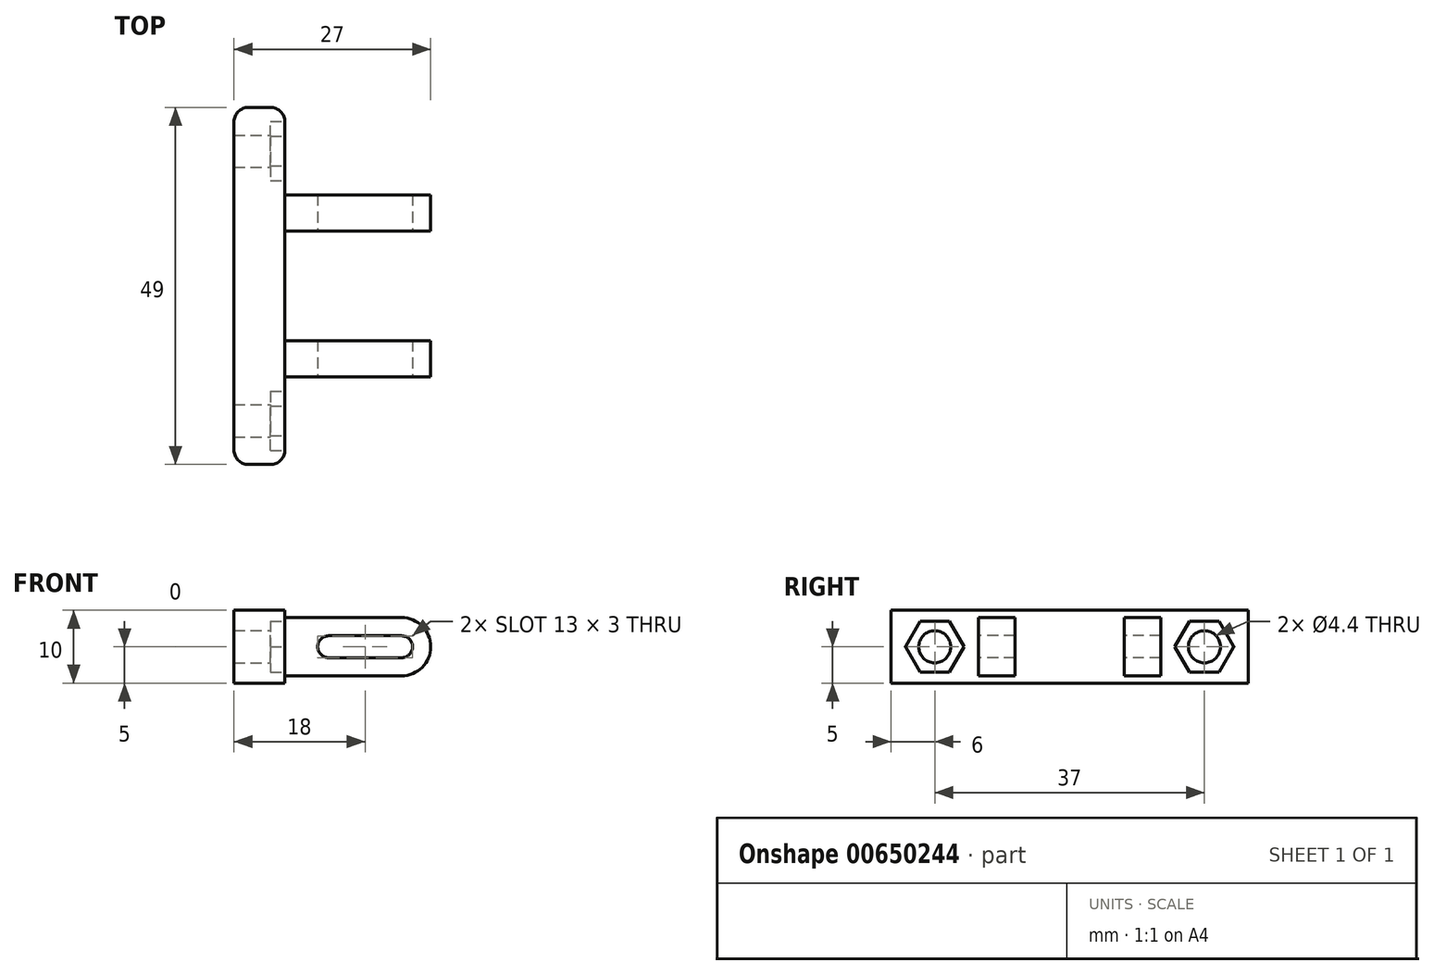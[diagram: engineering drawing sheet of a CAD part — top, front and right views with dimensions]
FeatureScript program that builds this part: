
annotation { "Feature Type Name" : "Feature", "Feature Type Description" : "" }
export const myFeature = defineFeature(function(context is Context, id is Id, definition is map)
    precondition{}
    {
        {
            var Q0;
            Q0=qCreatedBy(makeId("Top.planeOp"),FACE);
            var sketch = newSketch(context, id + "F0", { "sketchPlane" : qUnion([Q0])});
            skLineSegment(sketch, "E0", {"start": v(0, 0) * mm, "end": v(7, 0) * mm});
            skLineSegment(sketch, "E1", {"start": v(7, 0) * mm, "end": v(7, 12) * mm});
            skLineSegment(sketch, "E2", {"start": v(7, 12) * mm, "end": v(27, 12) * mm});
            skLineSegment(sketch, "E3", {"start": v(27, 12) * mm, "end": v(27, 17) * mm});
            skLineSegment(sketch, "E4", {"start": v(27, 17) * mm, "end": v(7, 17) * mm});
            skLineSegment(sketch, "E5", {"start": v(7, 17) * mm, "end": v(7, 32) * mm});
            skLineSegment(sketch, "E6", {"start": v(7, 32) * mm, "end": v(27, 32) * mm});
            skLineSegment(sketch, "E7", {"start": v(27, 32) * mm, "end": v(27, 37) * mm});
            skLineSegment(sketch, "E8", {"start": v(27, 37) * mm, "end": v(7, 37) * mm});
            skLineSegment(sketch, "E9", {"start": v(7, 37) * mm, "end": v(7, 49) * mm});
            skLineSegment(sketch, "E10", {"start": v(7, 49) * mm, "end": v(0, 49) * mm});
            skLineSegment(sketch, "E11", {"start": v(0, 49) * mm, "end": v(0, 0) * mm});
            skLineSegment(sketch, "E12", {"start": v(7, 12) * mm, "end": v(7, 17) * mm});
            skLineSegment(sketch, "E13", {"start": v(7, 32) * mm, "end": v(7, 37) * mm});
            skSolve(sketch);
        }
        {
            var Q0;
            Q0=makeQuery(id+"F0.imprint","IMPRINT",FACE,{"disambiguationData":[TD([[makeQuery(id+"F0.imprint","IMPRINT",EDGE,{"derivedFrom":sQuery(id+"F0.wireOp",EDGE,"E0")}),1.0]])]});
            extrude(context, id + "F1", {"entities" : qUnion([Q0]), "depth" : 10 * mm, "offsetDistance" : 25 * mm});
        }
        {
            var Q0;
            Q0=makeQuery(id+"F0.imprint","IMPRINT",FACE,{"disambiguationData":[TD([[makeQuery(id+"F0.imprint","IMPRINT",EDGE,{"derivedFrom":sQuery(id+"F0.wireOp",EDGE,"E2")}),1.0]])]});
            var Q1;
            Q1=makeQuery(id+"F0.imprint","IMPRINT",FACE,{"disambiguationData":[TD([[makeQuery(id+"F0.imprint","IMPRINT",EDGE,{"derivedFrom":sQuery(id+"F0.wireOp",EDGE,"E6")}),1.0]])]});
            extrude(context, id + "F2", {"entities" : qUnion([Q0, Q1]), "operationType" : NewBodyOperationType.ADD, "depth" : 9 * mm, "offsetDistance" : 25 * mm, "hasSecondDirection" : true, "secondDirectionOppositeDirection" : true, "secondDirectionDepth" : -1 * mm});
        }
        {
            var Q0;
            Q0=makeQuery(id+"F1.opExtrude","CAP_EDGE",EDGE,{"disambiguationData":[OSD([sQuery(id+"F0.wireOp",EDGE,"E3")])],"isStart":false});
            var Q1;
            Q1=makeQuery(id+"F1.opExtrude","CAP_EDGE",EDGE,{"disambiguationData":[OSD([sQuery(id+"F0.wireOp",EDGE,"E3")])],"isStart":true});
            var Q2;
            Q2=makeQuery(id+"F1.opExtrude","CAP_EDGE",EDGE,{"disambiguationData":[OSD([sQuery(id+"F0.wireOp",EDGE,"E7")])],"isStart":false});
            var Q3;
            Q3=makeQuery(id+"F1.opExtrude","CAP_EDGE",EDGE,{"disambiguationData":[OSD([sQuery(id+"F0.wireOp",EDGE,"E7")])],"isStart":true});
            var Q4;
            Q4=makeQuery(id+"F2.opExtrude","CAP_EDGE",EDGE,{"disambiguationData":[OSD([sQuery(id+"F0.wireOp",EDGE,"E3")])],"isStart":false});
            var Q5;
            Q5=makeQuery(id+"F2.opExtrude","CAP_EDGE",EDGE,{"disambiguationData":[OSD([sQuery(id+"F0.wireOp",EDGE,"E3")])],"isStart":true});
            var Q6;
            Q6=makeQuery(id+"F2.opExtrude","CAP_EDGE",EDGE,{"disambiguationData":[OSD([sQuery(id+"F0.wireOp",EDGE,"E7")])],"isStart":false});
            var Q7;
            Q7=makeQuery(id+"F2.opExtrude","CAP_EDGE",EDGE,{"disambiguationData":[OSD([sQuery(id+"F0.wireOp",EDGE,"E7")])],"isStart":true});
            fillet(context, id + "F3", {"entities" : qUnion([Q0, Q1, Q2, Q3, Q4, Q5, Q6, Q7]), "radius" : 4 * mm, "tangentPropagation" : true, "allowEdgeOverflow" : false});
        }
        {
            var Q0;
            Q0=makeQuery(id+"F2.opExtrude","SWEPT_FACE",FACE,{"disambiguationData":[OSD([sQuery(id+"F0.wireOp",EDGE,"E2")])]});
            var sketch = newSketch(context, id + "F4", { "sketchPlane" : qUnion([Q0])});
            skCircle(sketch, "E14", {"center": v(23, 5) * mm, "radius": 1.5 * mm});
            skCircle(sketch, "E15", {"center": v(13, 5) * mm, "radius": 1.5 * mm});
            skLineSegment(sketch, "E16", {"start": v(23, 3.5) * mm, "end": v(13, 3.5) * mm});
            skLineSegment(sketch, "E17", {"start": v(23, 6.5) * mm, "end": v(13, 6.5) * mm});
            skSolve(sketch);
        }
        {
            var Q0;
            Q0 = qSketchRegion(id + "F4", true);
            extrude(context, id + "F5", {"entities" : qUnion([Q0]), "operationType" : NewBodyOperationType.REMOVE, "oppositeDirection" : true, "depth" : 25 * mm, "offsetDistance" : 25 * mm});
        }
        {
            var Q0;
            Q0=makeQuery(id+"F1.opExtrude","SWEPT_FACE",FACE,{"disambiguationData":[OSD([sQuery(id+"F0.wireOp",EDGE,"E1")])]});
            var sketch = newSketch(context, id + "F6", { "sketchPlane" : qUnion([Q0])});
            skPoint(sketch, "E18.positionSnap0", {"position": v(0, 5) * mm});
            skLineSegment(sketch, "E19.0", {"start": v(49, 10) * mm, "end": v(49, 0) * mm, "construction": true});
            skLineSegment(sketch, "E20", {"start": v(49, 0) * mm, "end": v(0, 0) * mm, "construction": true});
            skLineSegment(sketch, "E21", {"start": v(12, 10) * mm, "end": v(0, 10) * mm, "construction": true});
            skLineSegment(sketch, "E22", {"start": v(6, 10) * mm, "end": v(6, 0) * mm, "construction": true});
            skCircle(sketch, "E23.cCircle", {"center": v(6, 5) * mm, "radius": 4.05 * mm, "construction": true});
            skPoint(sketch, "E23.cCircle.perimeterSnap0", {"position": v(6, 5) * mm});
            skLineSegment(sketch, "E23.0", {"start": v(10.05, 5) * mm, "end": v(8.03, 1.5) * mm});
            skPoint(sketch, "E23.0.startSnap0", {"position": v(6, 5) * mm});
            skLineSegment(sketch, "E23.1", {"start": v(8.03, 1.5) * mm, "end": v(3.98, 1.5) * mm});
            skLineSegment(sketch, "E23.2", {"start": v(3.98, 1.5) * mm, "end": v(1.95, 5) * mm});
            skLineSegment(sketch, "E23.3", {"start": v(1.95, 5) * mm, "end": v(3.97, 8.5) * mm});
            skLineSegment(sketch, "E23.4", {"start": v(3.97, 8.5) * mm, "end": v(8.02, 8.5) * mm});
            skLineSegment(sketch, "E23.5", {"start": v(8.02, 8.5) * mm, "end": v(10.05, 5) * mm});
            skLineSegment(sketch, "E24", {"start": v(24.5, 0) * mm, "end": v(24.5, 7.62) * mm, "construction": true});
            skPoint(sketch, "E25.MirrorP", {"position": v(43, 5) * mm});
            skLineSegment(sketch, "E26.MirrorCS", {"start": v(38.95, 5) * mm, "end": v(40.97, 1.5) * mm});
            skLineSegment(sketch, "E27.MirrorCS", {"start": v(40.98, 8.5) * mm, "end": v(38.95, 5) * mm});
            skLineSegment(sketch, "E28.MirrorCS", {"start": v(45.03, 8.5) * mm, "end": v(40.98, 8.5) * mm});
            skLineSegment(sketch, "E29.MirrorCS", {"start": v(47.05, 5) * mm, "end": v(45.03, 8.5) * mm});
            skLineSegment(sketch, "E30.MirrorCS", {"start": v(45.02, 1.5) * mm, "end": v(47.05, 5) * mm});
            skLineSegment(sketch, "E31.MirrorCS", {"start": v(40.97, 1.5) * mm, "end": v(45.02, 1.5) * mm});
            skSolve(sketch);
        }
        {
            var Q0;
            Q0=makeQuery(id+"F6.imprint","IMPRINT",FACE,{"disambiguationData":[TD([[makeQuery(id+"F6.imprint","IMPRINT",EDGE,{"derivedFrom":sQuery(id+"F6.wireOp",EDGE,"E23.0")}),-1.0]])]});
            var Q1;
            Q1=makeQuery(id+"F6.imprint","IMPRINT",FACE,{"disambiguationData":[TD([[makeQuery(id+"F6.imprint","IMPRINT",EDGE,{"derivedFrom":sQuery(id+"F6.wireOp",EDGE,"E26.MirrorCS")}),1.0]])]});
            extrude(context, id + "F7", {"entities" : qUnion([Q0, Q1]), "operationType" : NewBodyOperationType.REMOVE, "oppositeDirection" : true, "depth" : 2 * mm, "offsetDistance" : 25 * mm});
        }
        {
            var Q0;
            Q0=makeQuery(id+"F1.opExtrude","SWEPT_EDGE",EDGE,{"disambiguationData":[OSD([sQuery(id+"F0.wireOp",EDGE,"E0"),sQuery(id+"F0.wireOp",EDGE,"E11")])]});
            var Q1;
            Q1=makeQuery(id+"F1.opExtrude","SWEPT_EDGE",EDGE,{"disambiguationData":[OSD([sQuery(id+"F0.wireOp",EDGE,"E0"),sQuery(id+"F0.wireOp",EDGE,"E1")])]});
            var Q2;
            Q2=makeQuery(id+"F1.opExtrude","SWEPT_EDGE",EDGE,{"disambiguationData":[OSD([sQuery(id+"F0.wireOp",EDGE,"E10"),sQuery(id+"F0.wireOp",EDGE,"E11")])]});
            var Q3;
            Q3=makeQuery(id+"F1.opExtrude","SWEPT_EDGE",EDGE,{"disambiguationData":[OSD([sQuery(id+"F0.wireOp",EDGE,"E9"),sQuery(id+"F0.wireOp",EDGE,"E10")])]});
            var Q4;
            Q4=makeQuery(id+"F1.opExtrude","SWEPT_EDGE",EDGE,{"disambiguationData":[OSD([sQuery(id+"F0.wireOp",EDGE,"E5"),sQuery(id+"F0.wireOp",EDGE,"E6")])]});
            var Q5;
            Q5=makeQuery(id+"F1.opExtrude","SWEPT_EDGE",EDGE,{"disambiguationData":[OSD([sQuery(id+"F0.wireOp",EDGE,"E4"),sQuery(id+"F0.wireOp",EDGE,"E5")])]});
            var Q6;
            Q6=makeQuery(id+"F1.opExtrude","SWEPT_EDGE",EDGE,{"disambiguationData":[OSD([sQuery(id+"F0.wireOp",EDGE,"E1"),sQuery(id+"F0.wireOp",EDGE,"E2")])]});
            var Q7;
            Q7=makeQuery(id+"F1.opExtrude","SWEPT_EDGE",EDGE,{"disambiguationData":[OSD([sQuery(id+"F0.wireOp",EDGE,"E8"),sQuery(id+"F0.wireOp",EDGE,"E9")])]});
            var Q8;
            Q8=makeQuery(id+"F2.opExtrude","SWEPT_EDGE",EDGE,{"disambiguationData":[OSD([sQuery(id+"F0.wireOp",EDGE,"E1"),sQuery(id+"F0.wireOp",EDGE,"E2"),sQuery(id+"F0.wireOp",EDGE,"E12")])]});
            var Q9;
            Q9=makeQuery(id+"F2.opExtrude","SWEPT_EDGE",EDGE,{"disambiguationData":[OSD([sQuery(id+"F0.wireOp",EDGE,"E4"),sQuery(id+"F0.wireOp",EDGE,"E5"),sQuery(id+"F0.wireOp",EDGE,"E12")])]});
            var Q10;
            Q10=makeQuery(id+"F2.opExtrude","SWEPT_EDGE",EDGE,{"disambiguationData":[OSD([sQuery(id+"F0.wireOp",EDGE,"E5"),sQuery(id+"F0.wireOp",EDGE,"E6"),sQuery(id+"F0.wireOp",EDGE,"E13")])]});
            var Q11;
            Q11=makeQuery(id+"F2.opExtrude","SWEPT_EDGE",EDGE,{"disambiguationData":[OSD([sQuery(id+"F0.wireOp",EDGE,"E8"),sQuery(id+"F0.wireOp",EDGE,"E9"),sQuery(id+"F0.wireOp",EDGE,"E13")])]});
            var Q12;
            Q12=makeQuery(id+"F2.opExtrude","CAP_EDGE",EDGE,{"disambiguationData":[OSD([sQuery(id+"F0.wireOp",EDGE,"E13")])],"isStart":false});
            var Q13;
            Q13=makeQuery(id+"F2.opExtrude","CAP_EDGE",EDGE,{"disambiguationData":[OSD([sQuery(id+"F0.wireOp",EDGE,"E13")])],"isStart":true});
            var Q14;
            Q14=makeQuery(id+"F2.opExtrude","CAP_EDGE",EDGE,{"disambiguationData":[OSD([sQuery(id+"F0.wireOp",EDGE,"E12")])],"isStart":true});
            var Q15;
            Q15=makeQuery(id+"F2.opExtrude","CAP_EDGE",EDGE,{"disambiguationData":[OSD([sQuery(id+"F0.wireOp",EDGE,"E12")])],"isStart":false});
            fillet(context, id + "F8", {"entities" : qUnion([Q0, Q1, Q2, Q3, Q4, Q5, Q6, Q7, Q8, Q9, Q10, Q11, Q12, Q13, Q14, Q15]), "radius" : 2 * mm, "tangentPropagation" : true, "allowEdgeOverflow" : false});
        }
        {
            var Q0;
            Q0=sQuery(id+"F6.wireOp",VERTEX,"E23.0.startSnap0");
            var Q1;
            Q1=sQuery(id+"F6.wireOp",VERTEX,"E25.MirrorP");
            var Q2;
            Q2=makeQuery(id+"F1.opExtrude","SWEPT_BODY",BODY,{"disambiguationData":[OSD([sQuery(id+"F0.wireOp",EDGE,"E0"),sQuery(id+"F0.wireOp",EDGE,"E1"),sQuery(id+"F0.wireOp",EDGE,"E2"),sQuery(id+"F0.wireOp",EDGE,"E3"),sQuery(id+"F0.wireOp",EDGE,"E4"),sQuery(id+"F0.wireOp",EDGE,"E5"),sQuery(id+"F0.wireOp",EDGE,"E6"),sQuery(id+"F0.wireOp",EDGE,"E7"),sQuery(id+"F0.wireOp",EDGE,"E8"),sQuery(id+"F0.wireOp",EDGE,"E9"),sQuery(id+"F0.wireOp",EDGE,"E10"),sQuery(id+"F0.wireOp",EDGE,"E11")])]});
            hole(context, id + "F9", {"style" : HoleStyle.SIMPLE, "endStyle" : HoleEndStyle.THROUGH, "standardTappedOrClearance" : lookupTablePath({ "standard" : "ISO", "fit" : "Normal", "size" : "M4", "type" : "Clearance" }), "standardBlindInLast" : lookupTablePath({ "fit" : "Standard", "standard" : "ISO", "size" : "M4", "type" : "Clearance" }), "holeDiameter" : 4.4 * mm, "majorDiameter" : 4 * mm, "isTappedThrough" : true, "tappedDepth" : 5 * mm, "tapClearance" : 0, "locations" : qUnion([Q0, Q1]), "scope" : qUnion([Q2])});
        }
    });
